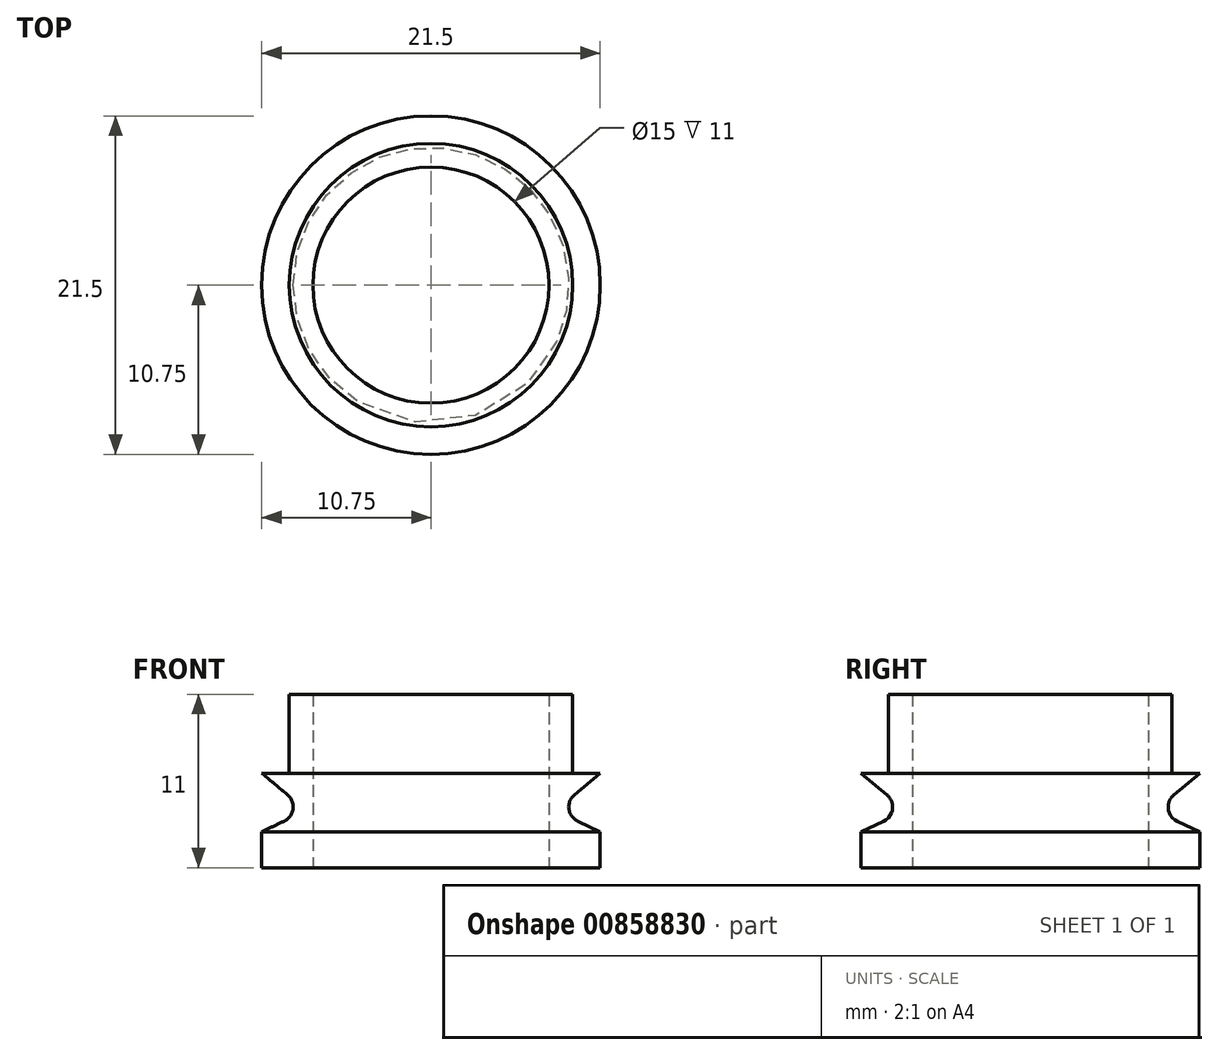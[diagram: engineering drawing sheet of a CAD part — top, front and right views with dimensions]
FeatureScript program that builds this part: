
annotation { "Feature Type Name" : "Feature", "Feature Type Description" : "" }
export const myFeature = defineFeature(function(context is Context, id is Id, definition is map)
    precondition{}
    {
        {
            var Q0;
            Q0=qCreatedBy(makeId("Front.planeOp"),FACE);
            var sketch = newSketch(context, id + "F0", { "sketchPlane" : qUnion([Q0])});
            skLineSegment(sketch, "E0", {"start": v(0, 0) * mm, "end": v(0, 27.07) * mm, "construction": true});
            skLineSegment(sketch, "E1", {"start": v(0, 0) * mm, "end": v(-7.5, 0) * mm, "construction": true});
            skLineSegment(sketch, "E2", {"start": v(-7.5, 0) * mm, "end": v(-10.75, 0) * mm});
            skLineSegment(sketch, "E3", {"start": v(-7.5, 0) * mm, "end": v(-7.5, 11) * mm});
            skLineSegment(sketch, "E4", {"start": v(-7.5, 11) * mm, "end": v(-9, 11) * mm});
            skLineSegment(sketch, "E5", {"start": v(-9, 11) * mm, "end": v(-9, 6) * mm});
            skLineSegment(sketch, "E6", {"start": v(-9, 6) * mm, "end": v(-10.75, 6) * mm});
            skLineSegment(sketch, "E7", {"start": v(-10.75, 6) * mm, "end": v(-10.75, 3.85) * mm, "construction": true});
            skLineSegment(sketch, "E8", {"start": v(-10.75, 3.85) * mm, "end": v(-9.75, 3.85) * mm, "construction": true});
            skLineSegment(sketch, "E9", {"start": v(-10.75, 3.85) * mm, "end": v(-10.75, 0) * mm});
            skLineSegment(sketch, "E10", {"start": v(-9.75, 3.85) * mm, "end": v(-10.75, 3.39) * mm, "construction": true});
            skLineSegment(sketch, "E11", {"start": v(-10.14, 0.95) * mm, "end": v(-10.75, 0.67) * mm, "construction": true});
            skLineSegment(sketch, "E12", {"start": v(-10.75, 0.67) * mm, "end": v(-9.32, 1.33) * mm});
            skLineSegment(sketch, "E13", {"start": v(-10.75, 0) * mm, "end": v(-10.75, 0.67) * mm});
            skLineSegment(sketch, "E14", {"start": v(-10.75, 6) * mm, "end": v(-9.1, 4.62) * mm});
            skLineSegment(sketch, "E15", {"start": v(-9.76, 1.13) * mm, "end": v(-11.18, 4.19) * mm, "construction": true});
            skLineSegment(sketch, "E16", {"start": v(-10.75, 2.29) * mm, "end": v(-9.33, 2.95) * mm});
            skArc(sketch, "E17", {"start": v(-9.33, 2.95) * mm, "mid": v(-8.76, 3.72) * mm, "end": v(-9.1, 4.62) * mm});
            skSolve(sketch);
        }
        {
            var Q0;
            Q0=makeQuery(id+"F0.imprint","IMPRINT",FACE,{"disambiguationData":[TD([[makeQuery(id+"F0.imprint","IMPRINT",EDGE,{"derivedFrom":sQuery(id+"F0.wireOp",EDGE,"E2")}),-1.0]])]});
            var Q1;
            Q1=sQuery(id+"F0.wireOp",EDGE,"E0");
            revolve(context, id + "F1", {"surfaceOperationType" : NewSurfaceOperationType.NEW, "entities" : qUnion([Q0]), "axis" : qUnion([Q1]), "revolveType" : RevolveType.FULL});
        }
    });
